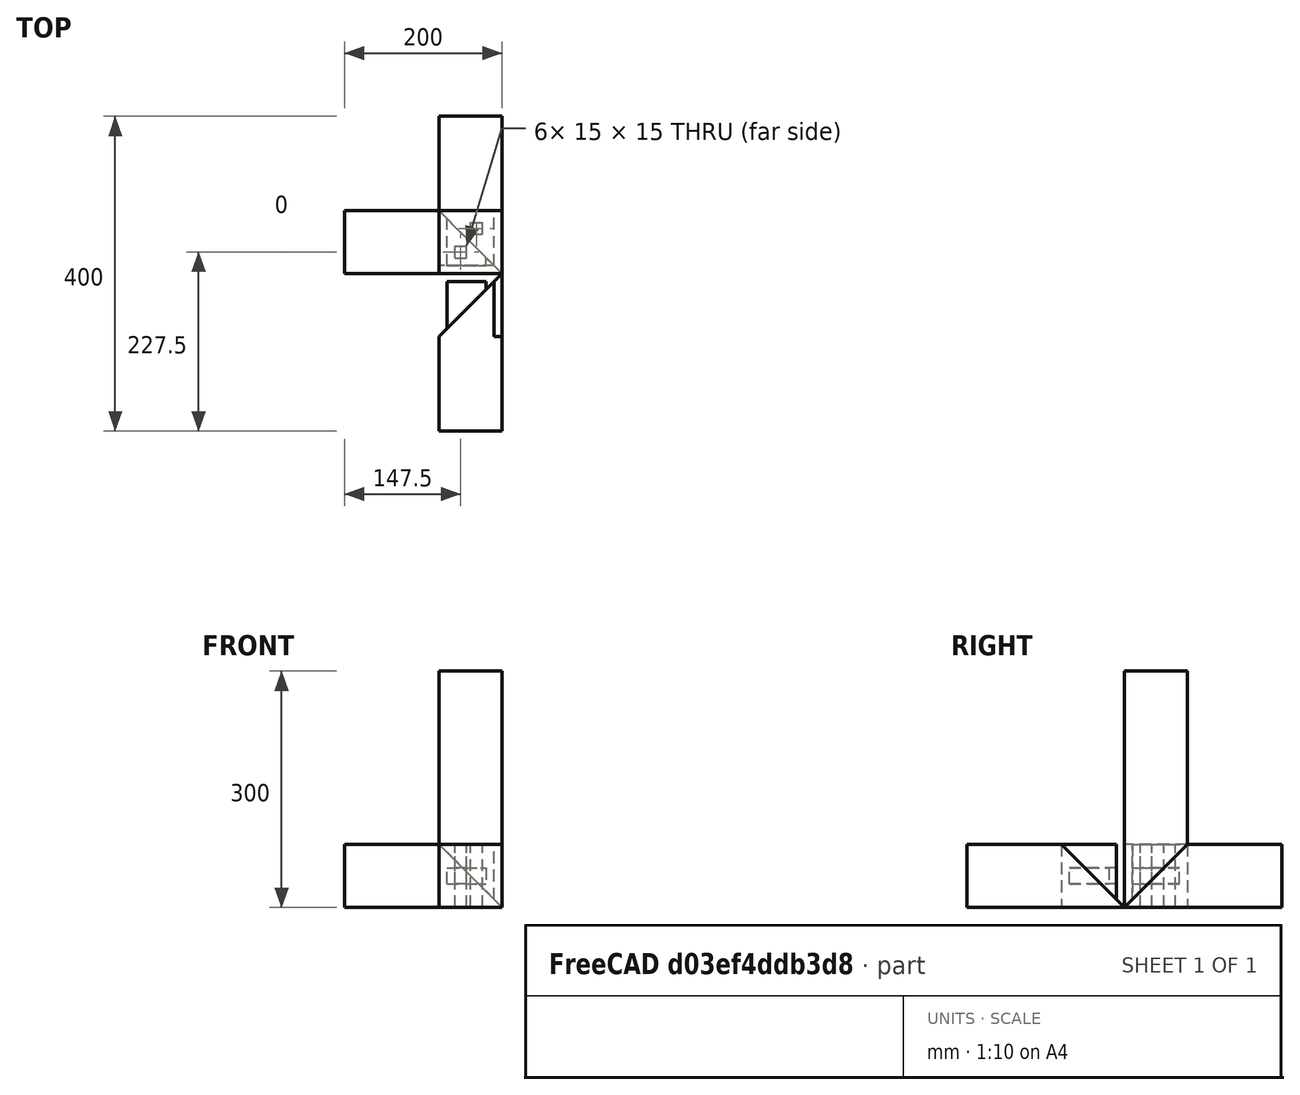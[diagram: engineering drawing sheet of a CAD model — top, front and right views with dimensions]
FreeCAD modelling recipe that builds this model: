
FCSTD DOCUMENT  (FreeCAD 0.18.2R)
Label: TRIPLE UNION
License: All rights reserved
LicenseURL: http://en.wikipedia.org/wiki/All_rights_reserved
objects: Part::Feature×8, Part::Cut×7, Part::Box×5, Part::MultiFuse×2, Part::Mirroring×1
note: 23 computed .brp shape members not serialized (recipe doc carries the construction recipe); baked Part::Feature solids carry a one-line shape summary decoded from their .brp

FEATURE [Part::Box] Box  label="Cube"
  AttacherType = Attacher::AttachEngine3D
  Height = 80
  Length = 80
  Width = 200
FEATURE [Part::Box] Box001  label="Cube001"
  AttacherType = Attacher::AttachEngine3D
  Height = 80
  Length = 10
  Placement = pos=(70,0,0) rot=(1,0,0;0.785398rad)
  Width = 120
FEATURE [Part::Cut] Cut
  Base = -> Box
  Tool = -> Box001
FEATURE [Part::Feature] Box002  label="Cube002"
  Placement = pos=(80,0,1.78e-14) rot=(-0.357407,0.862856,-0.357407;4.56541rad)
  shape: bbox 198 x 198 x 80 mm, 6 faces (baked)
FEATURE [Part::Cut] Cut001
  Base = -> Cut
  Tool = -> Box002
FEATURE [Part::Box] Box003  label="Cube003"
  AttacherType = Attacher::AttachEngine3D
  Height = 20
  Length = 50
  Placement = pos=(10,10,30) rot=(0,0,1;0rad)
  Width = 60
FEATURE [Part::MultiFuse] Fusion
  Shapes = -> [Box003,Cut001]
FEATURE [Part::Mirroring] Part__Mirroring  label="Fusion (Mirror #1)"
  Base = (0,0,0)
  Normal = (0,1,0)
  Source = -> Fusion
FEATURE [Part::Feature] Part__Mirroring001  label="Fusion (Mirror #1)001"
  Placement = pos=(80,80,0) rot=(0,0,1;4.71239rad)
  shape: bbox 200 x 80 x 80 mm, 13 faces (baked)
FEATURE [Part::Cut] Cut002
  Base = -> Part__Mirroring001
  Tool = -> Fusion
FEATURE [Part::Feature] Fusion001
  shape: bbox 80 x 200 x 80 mm, 13 faces (baked)
FEATURE [Part::Box] Box004  label="Cube004"
  AttacherType = Attacher::AttachEngine3D
  Height = 80
  Length = 15
  Placement = pos=(40,50,0) rot=(0,0,1;0rad)
  Width = 15
FEATURE [Part::Feature] Box004001  label="Cube005"
  Placement = pos=(20,20,0) rot=(0,0,1;0rad)
  shape: bbox 15 x 15 x 80 mm, 6 faces (baked)
FEATURE [Part::Cut] Cut003
  Base = -> Fusion001
  Tool = -> Box004
FEATURE [Part::Cut] Cut004
  Base = -> Cut002
  Tool = -> Box004001
FEATURE [Part::Feature] Box004001001  label="Cube006"
  Placement = pos=(20,20,0) rot=(0,0,1;0rad)
  shape: bbox 15 x 15 x 80 mm, 6 faces (baked)
FEATURE [Part::Cut] Cut005
  Base = -> Cut003
  Tool = -> Box004001001
FEATURE [Part::Box] Box004001002  label="Cube007"
  AttacherType = Attacher::AttachEngine3D
  Height = 300
  Length = 80
  Width = 80
FEATURE [Part::MultiFuse] Fusion002
  Shapes = -> [Cut004,Cut005]
FEATURE [Part::Cut] Cut006
  Base = -> Box004001002
  Tool = -> Fusion002
FEATURE [Part::Feature] Cut006001  label="Cut007"
  shape: bbox 80 x 80 x 300 mm, 20 faces (baked)
FEATURE [Part::Feature] Cut004001  label="Cut008"
  shape: bbox 200 x 80 x 80 mm, 21 faces (baked)
FEATURE [Part::Feature] Cut005001  label="Cut009"
  shape: bbox 80 x 200 x 80 mm, 21 faces (baked)
